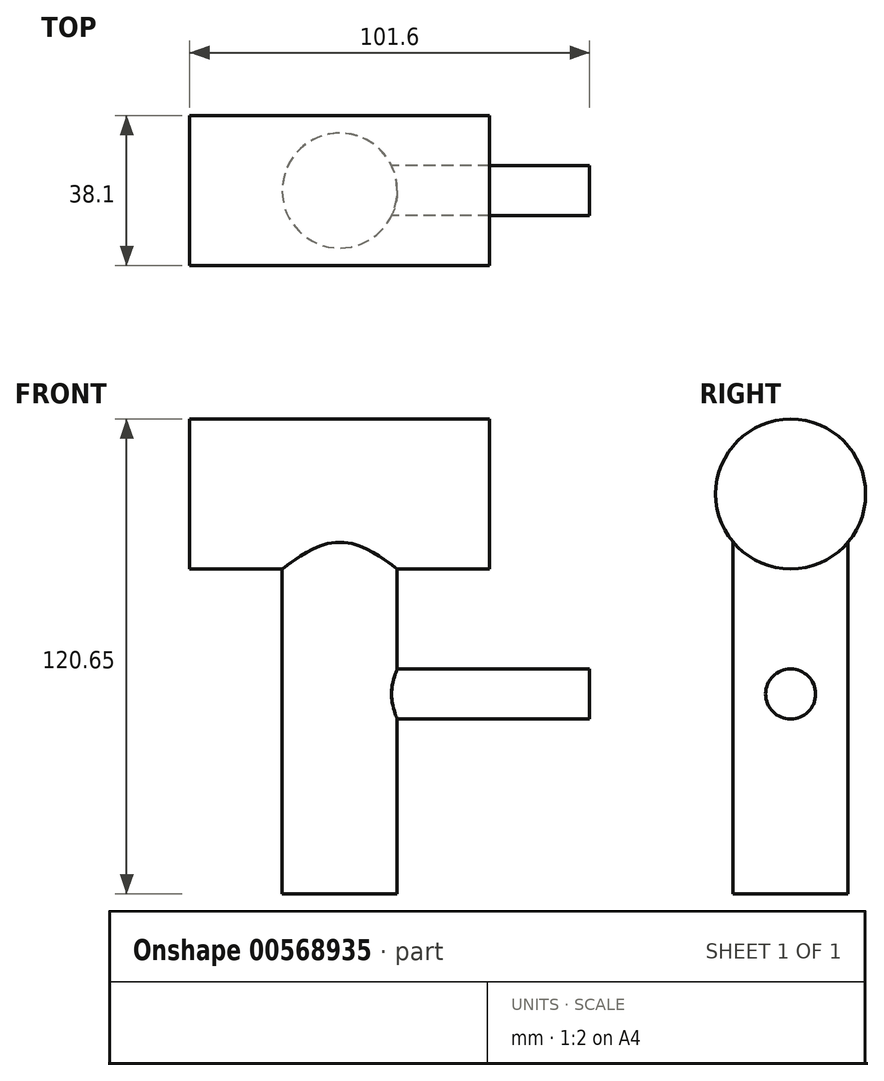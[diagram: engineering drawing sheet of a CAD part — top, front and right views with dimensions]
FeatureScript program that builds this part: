
annotation { "Feature Type Name" : "Feature", "Feature Type Description" : "" }
export const myFeature = defineFeature(function(context is Context, id is Id, definition is map)
    precondition{}
    {
        {
            var Q0;
            Q0=qCreatedBy(makeId("Right.planeOp"),FACE);
            var sketch = newSketch(context, id + "F0", { "sketchPlane" : qUnion([Q0])});
            skCircle(sketch, "E0", {"center": v(0, 0) * mm, "radius": 19.05 * mm});
            skSolve(sketch);
        }
        {
            var Q0;
            Q0 = qSketchRegion(id + "F0", true);
            extrude(context, id + "F1", {"entities" : qUnion([Q0]), "depth" : 76.2 * mm, "offsetDistance" : 25.4 * mm, "symmetric" : true});
        }
        {
            var Q0;
            Q0=qCreatedBy(makeId("Top.planeOp"),FACE);
            var sketch = newSketch(context, id + "F2", { "sketchPlane" : qUnion([Q0])});
            skCircle(sketch, "E1", {"center": v(0, 0) * mm, "radius": 14.6 * mm});
            skSolve(sketch);
        }
        {
            var Q0;
            Q0 = qSketchRegion(id + "F2", true);
            extrude(context, id + "F3", {"entities" : qUnion([Q0]), "operationType" : NewBodyOperationType.ADD, "oppositeDirection" : true, "depth" : 101.6 * mm, "offsetDistance" : 25.4 * mm});
        }
        {
            var Q0;
            Q0=qCreatedBy(makeId("Right.planeOp"),FACE);
            var sketch = newSketch(context, id + "F4", { "sketchPlane" : qUnion([Q0])});
            skCircle(sketch, "E2", {"center": v(0, -50.8) * mm, "radius": 6.35 * mm});
            skSolve(sketch);
        }
        {
            var Q0;
            Q0 = qSketchRegion(id + "F4", true);
            extrude(context, id + "F5", {"entities" : qUnion([Q0]), "operationType" : NewBodyOperationType.ADD, "depth" : 63.5 * mm, "offsetDistance" : 25.4 * mm});
        }
    });
